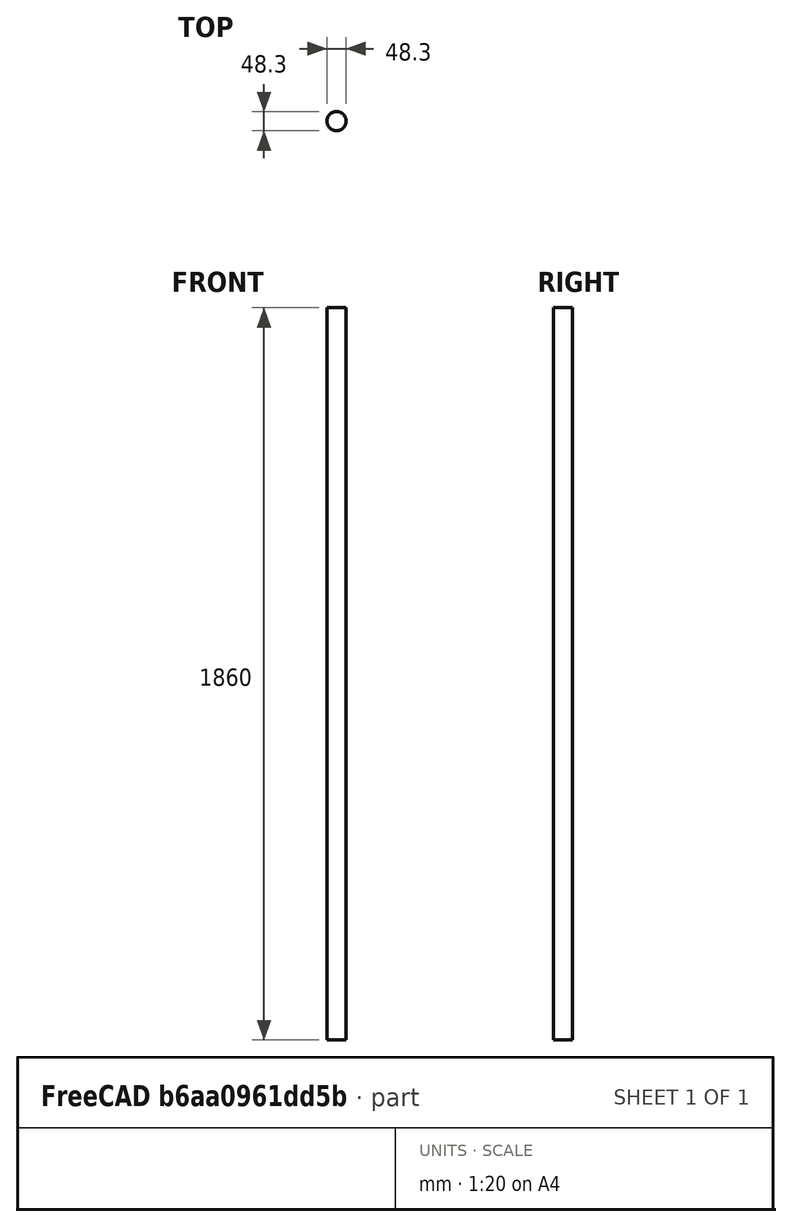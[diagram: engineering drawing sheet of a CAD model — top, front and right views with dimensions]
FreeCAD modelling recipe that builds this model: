
FCSTD DOCUMENT  (FreeCAD 0.21R33694 (Git))
Label: Tube_48mm_A
License: All rights reserved
LicenseURL: http://en.wikipedia.org/wiki/All_rights_reserved
objects: Sketcher::SketchObject×1, Part::Extrusion×1, Spreadsheet::Sheet×1
note: 2 computed .brp shape members not serialized (recipe doc carries the construction recipe); baked Part::Feature solids carry a one-line shape summary decoded from their .brp

FEATURE [Sketcher::SketchObject] Sketch  label="Tube_Circle_48_A1"
  FullyConstrained = false
  sketch-geometry (1):
    g0: Circle CenterX=0 CenterY=0 CenterZ=0 NormalX=0 NormalY=0 NormalZ=1 AngleXU=0 Radius=24.15
  constraints (1):
    c: Radius(g0) = 24.15
FEATURE [Part::Extrusion] Extrude  label="Tube_48_A1"
  Base = -> Sketch
  Dir = (0,0,1)
  DirMode = 2
  FaceMakerClass = Part::FaceMakerBullseye
  LengthFwd = 1860
  LengthRev = 0
  Solid = true
  Symmetric = false
  expr: LengthFwd = <<d>>.tubeA_length
FEATURE [Spreadsheet::Sheet] Spreadsheet  label="d"
  cells = A1='tubeA_length; B1(tubeA_length)==5700 / 3 - 20 * 2
